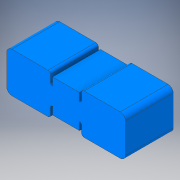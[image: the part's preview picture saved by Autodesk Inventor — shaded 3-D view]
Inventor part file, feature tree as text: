
AUTODESK INVENTOR PART (.ipt)
format: ipt  version: 2017 (Build 210142000, 142)  size: 151,040 bytes
history: native  units: in
note: dims shown in document units (in); Inventor stores cm internally (conversion verified against a paired STEP export)
features: extrude x1, sketch x1
ambient origin geometry x8: Origin, YZ Plane, XZ Plane, XY Plane, X Axis, Y Axis, Z Axis, Center Point
bodies: Solid1 (feature_tree)
feature tree (2):
  extrude  "Extrusion1"  Depth=0.85in
  sketch  "Sketch1"  dims[d1=0.39in d2=0.85in d3=0.22in d4=0.04in d5=0.32in d6=0.1in d7=0.05in d8=0.04in d9=0.926in d10=0.0in]
